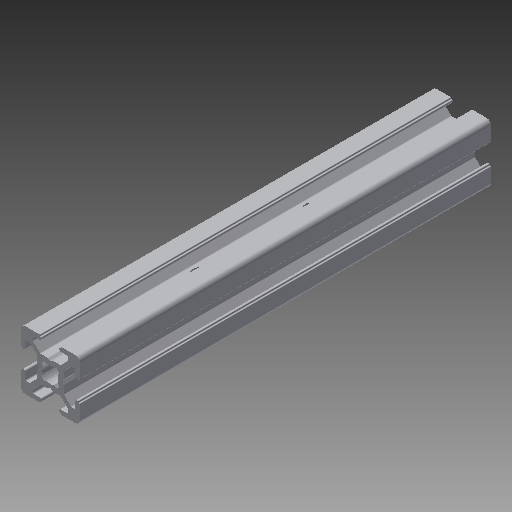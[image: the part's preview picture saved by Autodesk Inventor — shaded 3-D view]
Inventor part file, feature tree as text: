
AUTODESK INVENTOR PART (.ipt)
format: ipt  version: 2019 (Build 230136000, 136)  size: 414,720 bytes
history: native  units: in
note: dims shown in document units (in); Inventor stores cm internally (conversion verified against a paired STEP export)
features: other x3, sketch x2, extrude x1, hole x1, mirror x1
ambient origin geometry x8: Origin, YZ Plane, XZ Plane, XY Plane, X Axis, Y Axis, Z Axis, Center Point
bodies: Solid1 (feature_tree)
feature tree (8):
  other  "Blocks"
  extrude  "Extrusion1"  Depth=2.0in
  hole  "Hole1"  [1 undecoded]
  mirror  "Mirror1"
  sketch  "Sketch1"  dims[d1=0.0in d5=2.0in]
  other  "20x20"
  sketch  "Sketch3"  dims[d6=0.187in d7=0.75in d8=0.375in d9=0.25in d10=0.5635in d11=1.0in d12=0.8108in d13=1.0in d14=1.0in]
  other  "20x20:1"
note: 1 required parameter value undecoded (feature->parameter linkage not recoverable at this tier; creation-order binding heuristic only, values carry confidence <= 0.55)
